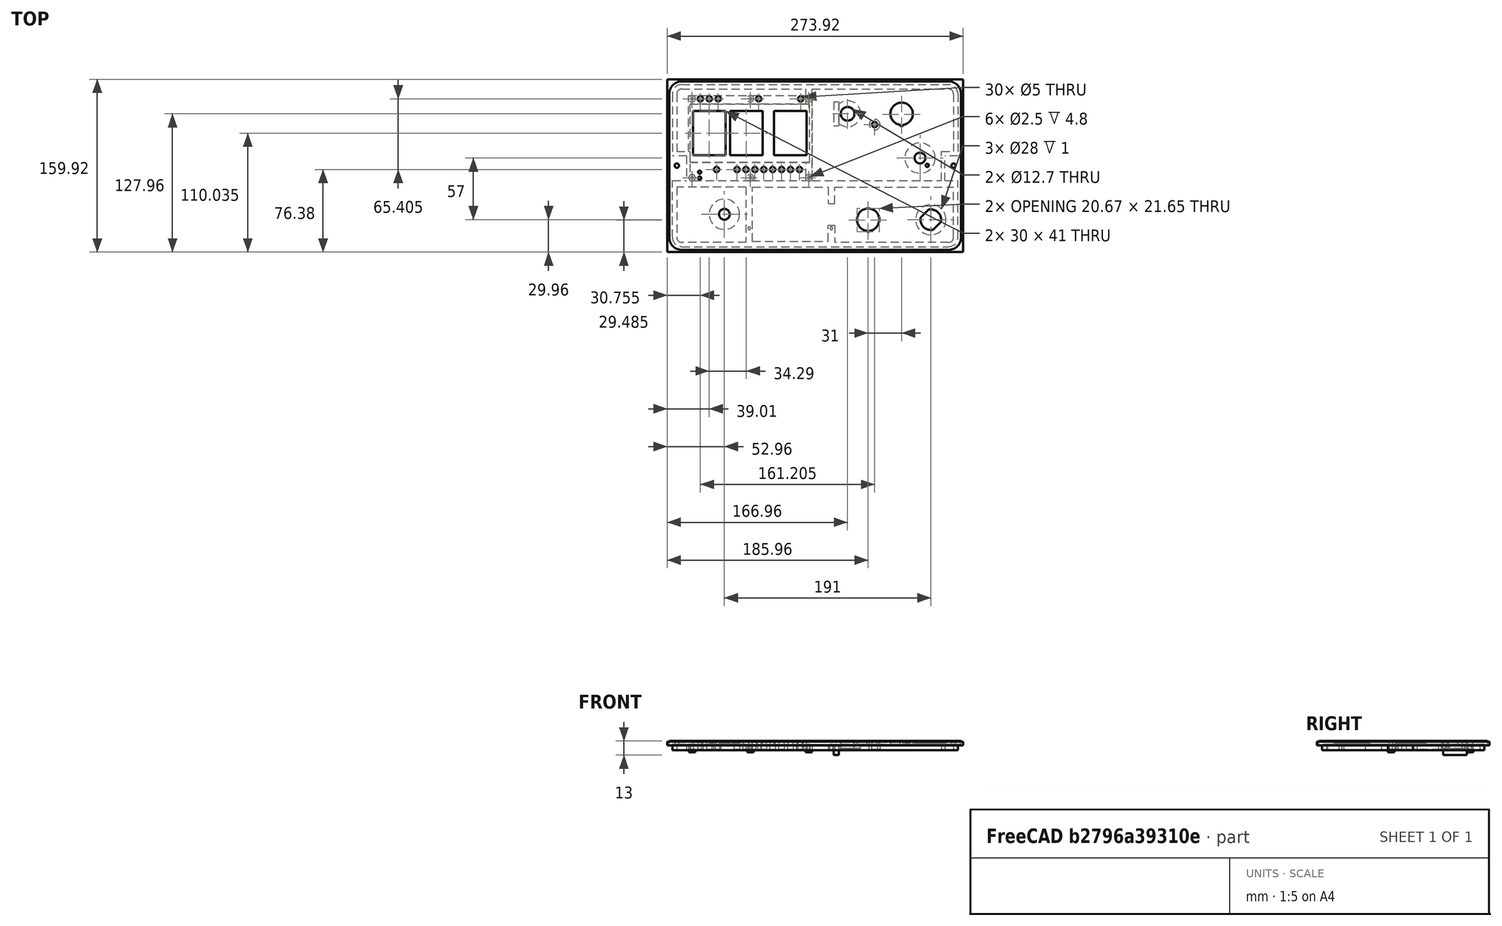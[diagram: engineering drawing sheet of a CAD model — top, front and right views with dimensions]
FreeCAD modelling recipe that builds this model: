
FCSTD DOCUMENT  (FreeCAD 0.18.1R)
Label: telelco_1170_panel
License: All rights reserved
LicenseURL: http://en.wikipedia.org/wiki/All_rights_reserved
objects: Sketcher::SketchObject×9, Part::Extrusion×9, Path::FeaturePython×4, Part::MultiFuse×2, Part::Cut×2, Part::FeaturePython×2, App::FeaturePython×1, Mesh::FeaturePython×1, App::DocumentObjectGroup×1, Path::FeatureCompoundPython×1
note: 26 computed .brp shape members not serialized (recipe doc carries the construction recipe); baked Part::Feature solids carry a one-line shape summary decoded from their .brp

FEATURE [Sketcher::SketchObject] Sketch  label="panel surface"
  MapMode = 5
  sketch-geometry (72):
    g0: Circle CenterX=-84 CenterY=-45 CenterZ=0 NormalX=0 NormalY=0 NormalZ=1 AngleXU=0 Radius=5
    g1: LineSegment [constr] StartX=-117 StartY=65 StartZ=0 EndX=-2.7 EndY=65 EndZ=0
    g2: LineSegment [constr] StartX=-2.7 StartY=65 StartZ=0 EndX=-2.7 EndY=-14.375 EndZ=0
    g3: LineSegment [constr] StartX=-2.7 StartY=-14.375 StartZ=0 EndX=-117 EndY=-14.375 EndZ=0
    g4: LineSegment [constr] StartX=-117 StartY=-14.375 StartZ=0 EndX=-117 EndY=65 EndZ=0
    g5: LineSegment StartX=-112.95 StartY=50.575 StartZ=0 EndX=-82.95 EndY=50.575 EndZ=0
    g6: LineSegment StartX=-82.95 StartY=50.575 StartZ=0 EndX=-82.95 EndY=9.575 EndZ=0
    g7: LineSegment StartX=-82.95 StartY=9.575 StartZ=0 EndX=-112.95 EndY=9.575 EndZ=0
    g8: LineSegment StartX=-112.95 StartY=9.575 StartZ=0 EndX=-112.95 EndY=50.575 EndZ=0
    g9: LineSegment [constr] StartX=-117 StartY=30.075 StartZ=0 EndX=-2.7 EndY=30.075 EndZ=0
    g10: LineSegment [constr] StartX=-97.95 StartY=65 StartZ=0 EndX=-97.95 EndY=-14.375 EndZ=0
    g11: LineSegment [constr] StartX=-63.66 StartY=65 StartZ=0 EndX=-63.66 EndY=-14.375 EndZ=0
    g12: LineSegment StartX=-78.66 StartY=50.575 StartZ=0 EndX=-48.66 EndY=50.575 EndZ=0
    g13: LineSegment StartX=-48.66 StartY=50.575 StartZ=0 EndX=-48.66 EndY=9.575 EndZ=0
    g14: LineSegment StartX=-48.66 StartY=9.575 StartZ=0 EndX=-78.66 EndY=9.575 EndZ=0
    g15: LineSegment StartX=-78.66 StartY=9.575 StartZ=0 EndX=-78.66 EndY=50.575 EndZ=0
    g16: LineSegment [constr] StartX=-23.02 StartY=65 StartZ=0 EndX=-23.02 EndY=-14.375 EndZ=0
    g17: LineSegment StartX=-38.02 StartY=50.575 StartZ=0 EndX=-8.02 EndY=50.575 EndZ=0
    g18: LineSegment StartX=-8.02 StartY=50.575 StartZ=0 EndX=-8.02 EndY=9.575 EndZ=0
    g19: LineSegment StartX=-8.02 StartY=9.575 StartZ=0 EndX=-38.02 EndY=9.575 EndZ=0
    g20: LineSegment StartX=-38.02 StartY=9.575 StartZ=0 EndX=-38.02 EndY=50.575 EndZ=0
    g21: LineSegment [constr] StartX=-117 StartY=61.825 StartZ=0 EndX=-2.7 EndY=61.825 EndZ=0
    g22: Circle CenterX=-106.205 CenterY=61.825 CenterZ=0 NormalX=0 NormalY=0 NormalZ=1 AngleXU=0 Radius=2.5
    g23: Circle CenterX=-97.95 CenterY=61.825 CenterZ=0 NormalX=0 NormalY=0 NormalZ=1 AngleXU=0 Radius=2.5
    g24: Circle CenterX=-89.695 CenterY=61.825 CenterZ=0 NormalX=0 NormalY=0 NormalZ=1 AngleXU=0 Radius=2.5
    g25: Circle CenterX=-52.23 CenterY=61.825 CenterZ=0 NormalX=0 NormalY=0 NormalZ=1 AngleXU=0 Radius=2.5
    g26: Circle CenterX=-13.368 CenterY=61.825 CenterZ=0 NormalX=0 NormalY=0 NormalZ=1 AngleXU=0 Radius=2.5
    g27: LineSegment [constr] StartX=-117 StartY=-3.58 StartZ=0 EndX=-2.7 EndY=-3.58 EndZ=0
    g28: Circle CenterX=-91.219 CenterY=-3.58 CenterZ=0 NormalX=0 NormalY=0 NormalZ=1 AngleXU=0 Radius=2.5
    g29: Circle CenterX=-72.296 CenterY=-3.58 CenterZ=0 NormalX=0 NormalY=0 NormalZ=1 AngleXU=0 Radius=2.5
    g30: Circle CenterX=-64.041 CenterY=-3.58 CenterZ=0 NormalX=0 NormalY=0 NormalZ=1 AngleXU=0 Radius=2.5
    g31: Circle CenterX=-55.786 CenterY=-3.58 CenterZ=0 NormalX=0 NormalY=0 NormalZ=1 AngleXU=0 Radius=2.5
    g32: Circle CenterX=-39.276 CenterY=-3.58 CenterZ=0 NormalX=0 NormalY=0 NormalZ=1 AngleXU=0 Radius=2.5
    g33: Circle CenterX=-22.766 CenterY=-3.58 CenterZ=0 NormalX=0 NormalY=0 NormalZ=1 AngleXU=0 Radius=2.5
    g34: Circle CenterX=-14.511 CenterY=-3.58 CenterZ=0 NormalX=0 NormalY=0 NormalZ=1 AngleXU=0 Radius=2.5
    g35: Circle CenterX=-31.021 CenterY=-3.58 CenterZ=0 NormalX=0 NormalY=0 NormalZ=1 AngleXU=0 Radius=2.5
    g36: Circle CenterX=-47.531 CenterY=-3.58 CenterZ=0 NormalX=0 NormalY=0 NormalZ=1 AngleXU=0 Radius=2.5
    g37: LineSegment [constr] StartX=-106.84 StartY=-3.58 StartZ=0 EndX=-106.84 EndY=-14.375 EndZ=0
    g38: Circle CenterX=-106.84 CenterY=-5.993 CenterZ=0 NormalX=0 NormalY=0 NormalZ=1 AngleXU=0 Radius=1.5
    g39: Circle CenterX=-106.84 CenterY=-11.5556 CenterZ=0 NormalX=0 NormalY=0 NormalZ=1 AngleXU=0 Radius=1.5
    g40: Circle [constr] CenterX=107 CenterY=-50 CenterZ=0 NormalX=0 NormalY=0 NormalZ=1 AngleXU=0 Radius=6.35
    g41: Circle CenterX=97 CenterY=7 CenterZ=0 NormalX=0 NormalY=0 NormalZ=1 AngleXU=0 Radius=5
    g42: Circle CenterX=-128 CenterY=0 CenterZ=0 NormalX=0 NormalY=0 NormalZ=1 AngleXU=0 Radius=2
    g43: Circle CenterX=128 CenterY=0 CenterZ=0 NormalX=0 NormalY=0 NormalZ=1 AngleXU=0 Radius=2
    g44: LineSegment [constr] StartX=30 StartY=48 StartZ=0 EndX=80 EndY=48 EndZ=0
    g45: Circle CenterX=30 CenterY=48 CenterZ=0 NormalX=0 NormalY=0 NormalZ=1 AngleXU=0 Radius=6.35
    g46: LineSegment [constr] StartX=55 StartY=48 StartZ=0 EndX=55 EndY=38 EndZ=0
    g47: Circle CenterX=55 CenterY=38 CenterZ=0 NormalX=0 NormalY=0 NormalZ=1 AngleXU=0 Radius=2.5
    g48: LineSegment [constr] StartX=97 StartY=7 StartZ=0 EndX=103.735 EndY=0.264808 EndZ=0
    g49: Circle CenterX=103.735 CenterY=0.264808 CenterZ=0 NormalX=0 NormalY=0 NormalZ=1 AngleXU=0 Radius=1.5
    g50: LineSegment StartX=47.85 StartY=-61.3 StartZ=0 EndX=50.15 EndY=-61.3 EndZ=0
    g51: LineSegment StartX=50.15 StartY=-61.3 StartZ=0 EndX=50.15 EndY=-60.2859 EndZ=0
    g52: LineSegment StartX=47.85 StartY=-61.3 StartZ=0 EndX=47.85 EndY=-60.2859 EndZ=0
    g53: ArcOfCircle CenterX=49 CenterY=-50 CenterZ=0 NormalX=0 NormalY=0 NormalZ=1 AngleXU=0 Radius=10.35 StartAngle=4.82373 EndAngle=10.8842
    g54: LineSegment StartX=78.85 StartY=36.7 StartZ=0 EndX=81.15 EndY=36.7 EndZ=0
    g55: LineSegment StartX=78.85 StartY=36.7 StartZ=0 EndX=78.85 EndY=37.7141 EndZ=0
    g56: LineSegment StartX=81.15 StartY=36.7 StartZ=0 EndX=81.15 EndY=37.7141 EndZ=0
    g57: ArcOfCircle CenterX=80 CenterY=48 CenterZ=0 NormalX=0 NormalY=0 NormalZ=1 AngleXU=0 Radius=10.35 StartAngle=4.82373 EndAngle=10.8842
    g58: ArcOfCircle CenterX=-123.32 CenterY=66.32 CenterZ=0 NormalX=0 NormalY=0 NormalZ=1 AngleXU=0 Radius=11.68 StartAngle=1.5708 EndAngle=3.14159
    g59: ArcOfCircle CenterX=123.32 CenterY=66.32 CenterZ=0 NormalX=0 NormalY=0 NormalZ=1 AngleXU=0 Radius=11.68 StartAngle=1.037e-13 EndAngle=1.5708
    g60: ArcOfCircle CenterX=123.32 CenterY=-66.32 CenterZ=0 NormalX=0 NormalY=0 NormalZ=1 AngleXU=0 Radius=11.68 StartAngle=4.71239 EndAngle=6.28319
    g61: ArcOfCircle CenterX=-123.32 CenterY=-66.32 CenterZ=0 NormalX=0 NormalY=0 NormalZ=1 AngleXU=0 Radius=11.68 StartAngle=3.14159 EndAngle=4.71239
    g62: LineSegment StartX=-123.32 StartY=78 StartZ=0 EndX=123.32 EndY=78 EndZ=0
    g63: LineSegment StartX=-135 StartY=66.32 StartZ=0 EndX=-135 EndY=-66.32 EndZ=0
    g64: LineSegment StartX=135 StartY=66.32 StartZ=0 EndX=135 EndY=-66.32 EndZ=0
    g65: LineSegment StartX=-123.32 StartY=-78 StartZ=0 EndX=123.32 EndY=-78 EndZ=0
    g66: LineSegment StartX=109.218 StartY=-59.2376 StartZ=0 EndX=116.238 EndY=-52.2176 EndZ=0
    g67: LineSegment StartX=97.7624 StartY=-47.7824 StartZ=0 EndX=104.782 EndY=-40.7624 EndZ=0
    g68: LineSegment [constr] StartX=107 StartY=-50 StartZ=0 EndX=112.728 EndY=-55.7276 EndZ=0
    g69: LineSegment [constr] StartX=107 StartY=-50 StartZ=0 EndX=101.272 EndY=-44.2724 EndZ=0
    g70: ArcOfCircle CenterX=107 CenterY=-50 CenterZ=0 NormalX=0 NormalY=0 NormalZ=1 AngleXU=0 Radius=9.5 StartAngle=6.04758 EndAngle=8.08958
    g71: ArcOfCircle CenterX=107 CenterY=-50 CenterZ=0 NormalX=0 NormalY=0 NormalZ=1 AngleXU=0 Radius=9.5 StartAngle=2.90599 EndAngle=4.94799
  constraints (210):
    c: Radius(g0) = 5
    c: Coincident(g1,g2)
    c: Coincident(g2,g3)
    c: Coincident(g3,g4)
    c: Coincident(g4,g1)
    c: Horizontal(g1)
    c: Horizontal(g3)
    c: Vertical(g2)
    c: Vertical(g4)
    c: DistanceX(g1,g1) = 114.3
    c: DistanceY(g2,g2) = 79.375
    c: Coincident(g5,g6)
    c: Coincident(g6,g7)
    c: Coincident(g7,g8)
    c: Coincident(g8,g5)
    c: Horizontal(g5)
    c: Horizontal(g7)
    c: Vertical(g8)
    c: DistanceX(g7,g7) = 30
    c: DistanceY(g6,g6) = 41
    c: PointOnObject(g9,g4)
    c: PointOnObject(g9,g2)
    c: DistanceY(g9,g1) = 34.925
    c: PointOnObject(g10,g1)
    c: PointOnObject(g10,g3)
    c: DistanceX(g10,g2) = 95.25
    c: Symmetric(g7,g6,g10)
    c: Symmetric(g6,g5,g9)
    c: PointOnObject(g11,g1)
    c: PointOnObject(g11,g3)
    c: Vertical(g11)
    c: DistanceX(g11,g2) = 60.96
    c: Coincident(g12,g13)
    c: Coincident(g13,g14)
    c: Coincident(g14,g15)
    c: Coincident(g15,g12)
    c: Horizontal(g12)
    c: Vertical(g13)
    c: Vertical(g15)
    c: Equal(g14,g7)
    c: Equal(g6,g15)
    c: Symmetric(g14,g13,g11)
    c: Symmetric(g12,g13,g9)
    c: PointOnObject(g16,g1)
    c: PointOnObject(g16,g3)
    c: Vertical(g16)
    c: DistanceX(g16,g2) = 20.32
    c: Coincident(g17,g18)
    c: Coincident(g18,g19)
    c: Coincident(g19,g20)
    c: Coincident(g20,g17)
    c: Horizontal(g17)
    c: Vertical(g20)
    c: Equal(g17,g12)
    c: Equal(g13,g20)
    c: Symmetric(g19,g18,g16)
    c: Symmetric(g18,g17,g9)
    c: PointOnObject(g21,g4)
    c: PointOnObject(g21,g2)
    c: Horizontal(g21)
    c: DistanceY(g21,g1) = 3.175
    c: PointOnObject(g22,g21)
    c: Radius(g22) = 2.5
    c: DistanceX(g22,g21) = 103.505
    c: PointOnObject(g23,g21)
    c: PointOnObject(g24,g21)
    c: PointOnObject(g25,g21)
    c: PointOnObject(g26,g21)
    c: Equal(g22,g23)
    c: Equal(g23,g24)
    c: Equal(g24,g25)
    c: Equal(g25,g26)
    c: DistanceX(g26,g21) = 10.668
    c: DistanceX(g25,g21) = 49.53
    c: DistanceX(g24,g21) = 86.995
    c: DistanceX(g23,g21) = 95.25
    c: PointOnObject(g27,g4)
    c: PointOnObject(g27,g2)
    c: Horizontal(g27)
    c: DistanceY(g27,g1) = 68.58
    c: PointOnObject(g28,g27)
    c: PointOnObject(g29,g27)
    c: PointOnObject(g30,g27)
    c: PointOnObject(g31,g27)
    c: PointOnObject(g32,g27)
    c: PointOnObject(g33,g27)
    c: PointOnObject(g34,g27)
    c: Equal(g28,g29)
    c: Equal(g33,g34)
    c: Equal(g34,g22)
    c: PointOnObject(g35,g27)
    c: PointOnObject(g36,g27)
    c: Equal(g36,g32)
    c: Equal(g32,g35)
    c: DistanceX(g34,g27) = 11.811
    c: DistanceX(g33,g27) = 20.066
    c: DistanceX(g35,g27) = 28.321
    c: DistanceX(g32,g27) = 36.576
    c: DistanceX(g36,g27) = 44.831
    c: DistanceX(g31,g27) = 53.086
    c: DistanceX(g30,g27) = 61.341
    c: DistanceX(g29,g27) = 69.596
    c: DistanceX(g28,g27) = 88.519
    c: PointOnObject(g37,g27)
    c: PointOnObject(g37,g3)
    c: Vertical(g37)
    c: DistanceX(g37,g2) = 104.14
    c: PointOnObject(g38,g37)
    c: PointOnObject(g39,g37)
    c: Equal(g38,g39)
    c: Radius(g38) = 1.5
    c: DistanceY(g38,g1) = 70.993
    c: DistanceY(g39,g1) = 76.5556
    c: Radius(g40) = 6.35
    c: PointOnObject(g42,g-1)
    c: PointOnObject(g43,g-1)
    c: Radius(g42) = 2
    c: Equal(g42,g43)
    c: Horizontal(g44)
    c: Coincident(g45,g44)
    c: Equal(g45,g40)
    c: Equal(g41,g0)
    c: DistanceX(g44,g44) = 50
    c: DistanceY(g-1,g44) = 48
    c: DistanceY(g-1,g1) = 65
    c: Vertical(g46)
    c: DistanceY(g46,g46) = 10
    c: Symmetric(g44,g44,g46)
    c: Coincident(g47,g46)
    c: Equal(g26,g47)
    c: Coincident(g48,g41)
    c: Distance(g48) = 9.525
    c: Angle(g48) = -0.785398
    c: Coincident(g49,g48)
    c: Radius(g49) = 1.5
    c: DistanceY(g40,g-1) = 50
    c: DistanceX(g50,g50) = 2.3
    c: Coincident(g51,g50)
    c: Vertical(g51)
    c: Coincident(g52,g50)
    c: Vertical(g52)
    c: Coincident(g53,g52)
    c: Coincident(g53,g51)
    c: Radius(g53) = 10.35
    c: DistanceY(g50,g53) = 11.3
    c: Horizontal(g54)
    c: DistanceX(g54,g54) = 2.3
    c: DistanceY(g54,g44) = 11.3
    c: Coincident(g55,g54)
    c: Vertical(g55)
    c: Coincident(g56,g54)
    c: Vertical(g56)
    c: Coincident(g57,g44)
    c: Coincident(g57,g55)
    c: Coincident(g57,g56)
    c: Radius(g57) = 10.35
    c: Equal(g33,g35)
    c: Equal(g36,g31)
    c: Equal(g31,g30)
    c: Equal(g30,g29)
    c: DistanceX(g53,g40) = 58
    c: Horizontal(g50)
    c: Horizontal(g52,g51)
    c: Horizontal(g55,g56)
    c: Horizontal(g53,g40)
    c: DistanceX(g2,g-1) = 2.7
    c: DistanceX(g0,g-1) = 84
    c: DistanceY(g0,g-1) = 45
    c: DistanceX(g-1,g53) = 49
    c: DistanceX(g-1,g44) = 30
    c: DistanceX(g-1,g41) = 97
    c: DistanceY(g-1,g41) = 7
    c: DistanceX(g-1,g43) = 128
    c: DistanceX(g42,g-1) = 128
    c: Radius(g58) = 11.68
    c: Equal(g58,g59)
    c: Equal(g59,g60)
    c: Equal(g60,g61)
    c: Horizontal(g62)
    c: Tangent(g59,g62) = 1.5708
    c: Tangent(g62,g58) = 1.5708
    c: Vertical(g64)
    c: Tangent(g64,g59) = 1.5708
    c: Tangent(g63,g58) = -1.5708
    c: DistanceX(g58,g59) = 270
    c: Symmetric(g58,g59,g-2)
    c: Tangent(g63,g61) = -1.5708
    c: Tangent(g65,g61) = -1.5708
    c: DistanceY(g61,g58) = 156
    c: Symmetric(g61,g58,g-1)
    c: Tangent(g60,g65) = -1.5708
    c: Tangent(g60,g64) = 1.5708
    c: Angle(g66,g65) = 2.35619
    c: Parallel(g67,g66)
    c: Coincident(g68,g40)
    c: PointOnObject(g68,g66)
    c: Perpendicular(g68,g66)
    c: Distance(g68) = 8.1
    c: Coincident(g69,g40)
    c: PointOnObject(g69,g67)
    c: Perpendicular(g69,g67)
    c: Equal(g69,g68)
    c: Coincident(g70,g40)
    c: Coincident(g70,g67)
    c: Coincident(g70,g66)
    c: Coincident(g71,g40)
    c: Coincident(g71,g66)
    c: Coincident(g71,g67)
    c: Diameter(g70) = 19
    c: Equal(g71,g70)
FEATURE [Sketcher::SketchObject] Sketch002  label="pcb mounts"
  MapMode = 5
  sketch-geometry (18):
    g0: LineSegment [constr] StartX=-117 StartY=65 StartZ=0 EndX=-2.7 EndY=65 EndZ=0
    g1: LineSegment [constr] StartX=-2.7 StartY=65 StartZ=0 EndX=-2.7 EndY=-14.375 EndZ=0
    g2: LineSegment [constr] StartX=-2.7 StartY=-14.375 StartZ=0 EndX=-117 EndY=-14.375 EndZ=0
    g3: LineSegment [constr] StartX=-117 StartY=-14.375 StartZ=0 EndX=-117 EndY=65 EndZ=0
    g4: LineSegment [constr] StartX=-117 StartY=61.825 StartZ=0 EndX=-2.7 EndY=61.825 EndZ=0
    g5: LineSegment [constr] StartX=-117 StartY=-11.2 StartZ=0 EndX=-2.7 EndY=-11.2 EndZ=0
    g6: Circle CenterX=-5.875 CenterY=61.825 CenterZ=0 NormalX=0 NormalY=0 NormalZ=1 AngleXU=0 Radius=1.25
    g7: Circle CenterX=-5.875 CenterY=61.825 CenterZ=0 NormalX=0 NormalY=0 NormalZ=1 AngleXU=0 Radius=3
    g8: Circle CenterX=-59.85 CenterY=61.825 CenterZ=0 NormalX=0 NormalY=0 NormalZ=1 AngleXU=0 Radius=3
    g9: Circle CenterX=-59.85 CenterY=61.825 CenterZ=0 NormalX=0 NormalY=0 NormalZ=1 AngleXU=0 Radius=1.25
    g10: Circle CenterX=-113.825 CenterY=61.825 CenterZ=0 NormalX=0 NormalY=0 NormalZ=1 AngleXU=0 Radius=1.25
    g11: Circle CenterX=-113.825 CenterY=61.825 CenterZ=0 NormalX=0 NormalY=0 NormalZ=1 AngleXU=0 Radius=3
    g12: Circle CenterX=-113.825 CenterY=-11.2 CenterZ=0 NormalX=0 NormalY=0 NormalZ=1 AngleXU=0 Radius=1.25
    g13: Circle CenterX=-113.825 CenterY=-11.2 CenterZ=0 NormalX=0 NormalY=0 NormalZ=1 AngleXU=0 Radius=3
    g14: Circle CenterX=-59.85 CenterY=-11.2 CenterZ=0 NormalX=0 NormalY=0 NormalZ=1 AngleXU=0 Radius=1.25
    g15: Circle CenterX=-59.85 CenterY=-11.2 CenterZ=0 NormalX=0 NormalY=0 NormalZ=1 AngleXU=0 Radius=3
    g16: Circle CenterX=-5.875 CenterY=-11.2 CenterZ=0 NormalX=0 NormalY=0 NormalZ=1 AngleXU=0 Radius=1.25
    g17: Circle CenterX=-5.875 CenterY=-11.2 CenterZ=0 NormalX=0 NormalY=0 NormalZ=1 AngleXU=0 Radius=3
  constraints (50):
    c: Coincident(g1,g2)
    c: Coincident(g2,g3)
    c: Coincident(g3,g0)
    c: Horizontal(g0)
    c: Horizontal(g2)
    c: Vertical(g1)
    c: Vertical(g3)
    c: DistanceX(g0,g0) = 114.3
    c: DistanceY(g1,g1) = 79.375
    c: PointOnObject(g4,g3)
    c: PointOnObject(g4,g1)
    c: Horizontal(g4)
    c: DistanceY(g4,g0) = 3.175
    c: PointOnObject(g5,g3)
    c: PointOnObject(g5,g1)
    c: Horizontal(g5)
    c: DistanceY(g5,g0) = 76.2
    c: DistanceX(g1,g-1) = 2.7
    c: Coincident(g1,g0)
    c: DistanceY(g-1,g0) = 65
    c: PointOnObject(g6,g4)
    c: Radius(g6) = 1.25
    c: Coincident(g7,g6)
    c: Radius(g7) = 3
    c: DistanceX(g6,g4) = 3.175
    c: PointOnObject(g8,g4)
    c: Coincident(g9,g8)
    c: Equal(g9,g6)
    c: Equal(g8,g7)
    c: DistanceX(g8,g4) = 57.15
    c: PointOnObject(g10,g4)
    c: Coincident(g11,g10)
    c: Equal(g10,g9)
    c: Equal(g11,g8)
    c: DistanceX(g10,g4) = 111.125
    c: PointOnObject(g12,g5)
    c: Coincident(g13,g12)
    c: Equal(g12,g10)
    c: Equal(g13,g11)
    c: PointOnObject(g14,g5)
    c: Coincident(g15,g14)
    c: PointOnObject(g16,g5)
    c: Coincident(g17,g16)
    c: Equal(g14,g9)
    c: Equal(g8,g15)
    c: Equal(g6,g16)
    c: Equal(g7,g17)
    c: Vertical(g8,g14)
    c: Vertical(g10,g12)
    c: Vertical(g6,g16)
FEATURE [Part::Extrusion] Extrude002  label="Extrude pcb mounts"
  Base = -> Sketch002
  Dir = (0,0,1)
  DirMode = 2
  FaceMakerClass = Part::FaceMakerBullseye
  LengthFwd = 7.5
  LengthRev = 0
  Reversed = true
  Solid = true
  Symmetric = false
FEATURE [Sketcher::SketchObject] Sketch003  label="ribs"
  MapMode = 5
  sketch-geometry (60):
    g0: LineSegment [constr] StartX=-123.32 StartY=78 StartZ=0 EndX=123.32 EndY=78 EndZ=0
    g1: LineSegment [constr] StartX=-123.32 StartY=-78 StartZ=0 EndX=123.32 EndY=-78 EndZ=0
    g2: LineSegment [constr] StartX=-135 StartY=-66.32 StartZ=0 EndX=-135 EndY=66.32 EndZ=0
    g3: ArcOfCircle [constr] CenterX=-123.32 CenterY=66.32 CenterZ=0 NormalX=0 NormalY=0 NormalZ=1 AngleXU=0 Radius=11.68 StartAngle=1.5708 EndAngle=3.14159
    g4: ArcOfCircle [constr] CenterX=123.32 CenterY=66.32 CenterZ=0 NormalX=0 NormalY=0 NormalZ=1 AngleXU=0 Radius=11.68 StartAngle=-1.039e-13 EndAngle=1.5708
    g5: ArcOfCircle [constr] CenterX=123.32 CenterY=-66.32 CenterZ=0 NormalX=0 NormalY=0 NormalZ=1 AngleXU=0 Radius=11.68 StartAngle=4.71239 EndAngle=6.28319
    g6: ArcOfCircle [constr] CenterX=-123.32 CenterY=-66.32 CenterZ=0 NormalX=0 NormalY=0 NormalZ=1 AngleXU=0 Radius=11.68 StartAngle=3.14159 EndAngle=4.71239
    g7: ArcOfCircle CenterX=123.32 CenterY=66.32 CenterZ=0 NormalX=0 NormalY=0 NormalZ=1 AngleXU=0 Radius=4.68 StartAngle=4e-16 EndAngle=1.5708
    g8: ArcOfCircle CenterX=-123.32 CenterY=66.32 CenterZ=0 NormalX=0 NormalY=0 NormalZ=1 AngleXU=0 Radius=4.68 StartAngle=1.5708 EndAngle=3.14159
    g9: ArcOfCircle CenterX=-123.32 CenterY=-66.32 CenterZ=0 NormalX=0 NormalY=0 NormalZ=1 AngleXU=0 Radius=4.68 StartAngle=3.14159 EndAngle=4.71239
    g10: LineSegment StartX=-119 StartY=9 StartZ=0 EndX=-119 EndY=-14 EndZ=0
    g11: LineSegment StartX=-128 StartY=66.32 StartZ=0 EndX=-128 EndY=13 EndZ=0
    g12: LineSegment [constr] StartX=135 StartY=-66.32 StartZ=0 EndX=135 EndY=66.32 EndZ=0
    g13: LineSegment StartX=-64 StartY=-71 StartZ=0 EndX=-123.32 EndY=-71 EndZ=0
    g14: LineSegment StartX=-2.7 StartY=71 StartZ=0 EndX=123.32 EndY=71 EndZ=0
    g15: LineSegment StartX=-128 StartY=-20 StartZ=0 EndX=-128 EndY=-66.32 EndZ=0
    g16: LineSegment StartX=-123.32 StartY=71 StartZ=0 EndX=-8.7 EndY=71 EndZ=0
    g17: LineSegment StartX=-116 StartY=-14 StartZ=0 EndX=-8.7 EndY=-14 EndZ=0
    g18: LineSegment StartX=-2.7 StartY=-14 StartZ=0 EndX=-2.7 EndY=71 EndZ=0
    g19: LineSegment StartX=-8.7 StartY=-14 StartZ=0 EndX=-8.7 EndY=71 EndZ=0
    g20: LineSegment StartX=-58 StartY=-70 StartZ=0 EndX=12 EndY=-70 EndZ=0
    g21: LineSegment StartX=12 StartY=-70 StartZ=0 EndX=12 EndY=-55 EndZ=0
    g22: LineSegment StartX=12 StartY=-20 StartZ=0 EndX=12 EndY=-35 EndZ=0
    g23: LineSegment StartX=-58 StartY=-70 StartZ=0 EndX=-58 EndY=-20 EndZ=0
    g24: LineSegment StartX=-64 StartY=-20 StartZ=0 EndX=-64 EndY=-71 EndZ=0
    g25: LineSegment StartX=-58 StartY=-20 StartZ=0 EndX=12 EndY=-20 EndZ=0
    g26: LineSegment StartX=-64 StartY=-20 StartZ=0 EndX=-128 EndY=-20 EndZ=0
    g27: LineSegment StartX=18 StartY=-55 StartZ=0 EndX=18 EndY=-71 EndZ=0
    g28: LineSegment StartX=12 StartY=-55 StartZ=0 EndX=18 EndY=-55 EndZ=0
    g29: ArcOfCircle CenterX=123.32 CenterY=-66.32 CenterZ=0 NormalX=0 NormalY=0 NormalZ=1 AngleXU=0 Radius=4.68 StartAngle=4.71239 EndAngle=6.28319
    g30: LineSegment StartX=128 StartY=-66.32 StartZ=0 EndX=128 EndY=-20 EndZ=0
    g31: LineSegment StartX=123.32 StartY=-71 StartZ=0 EndX=18 EndY=-71 EndZ=0
    g32: LineSegment StartX=12 StartY=-35 StartZ=0 EndX=18 EndY=-35 EndZ=0
    g33: LineSegment StartX=18 StartY=-35 StartZ=0 EndX=18 EndY=-20 EndZ=0
    g34: LineSegment StartX=18 StartY=-20 StartZ=0 EndX=128 EndY=-20 EndZ=0
    g35: Circle CenterX=-5.875 CenterY=61.825 CenterZ=0 NormalX=0 NormalY=0 NormalZ=1 AngleXU=0 Radius=1.25
    g36: Circle CenterX=-5.875 CenterY=-11.2 CenterZ=0 NormalX=0 NormalY=0 NormalZ=1 AngleXU=0 Radius=1.25
    g37: Circle CenterX=-61 CenterY=-58 CenterZ=0 NormalX=0 NormalY=0 NormalZ=1 AngleXU=0 Radius=1.25
    g38: Circle CenterX=15 CenterY=-58 CenterZ=0 NormalX=0 NormalY=0 NormalZ=1 AngleXU=0 Radius=1.25
    g39: LineSegment StartX=-123.32 StartY=-75 StartZ=0 EndX=123.32 EndY=-75 EndZ=0
    g40: LineSegment StartX=-123.32 StartY=75 StartZ=0 EndX=123.32 EndY=75 EndZ=0
    g41: ArcOfCircle CenterX=123.32 CenterY=-66.32 CenterZ=0 NormalX=0 NormalY=0 NormalZ=1 AngleXU=0 Radius=8.68 StartAngle=4.71239 EndAngle=6.28319
    g42: ArcOfCircle CenterX=-123.32 CenterY=-66.32 CenterZ=0 NormalX=0 NormalY=0 NormalZ=1 AngleXU=0 Radius=8.68 StartAngle=3.14159 EndAngle=4.71239
    g43: ArcOfCircle CenterX=123.32 CenterY=66.32 CenterZ=0 NormalX=0 NormalY=0 NormalZ=1 AngleXU=0 Radius=8.68 StartAngle=-2.1239e-11 EndAngle=1.5708
    g44: ArcOfCircle CenterX=-123.32 CenterY=66.32 CenterZ=0 NormalX=0 NormalY=0 NormalZ=1 AngleXU=0 Radius=8.68 StartAngle=1.5708 EndAngle=3.14159
    g45: LineSegment StartX=132 StartY=66.32 StartZ=0 EndX=132 EndY=9 EndZ=0
    g46: LineSegment StartX=120 StartY=-14 StartZ=0 EndX=120 EndY=9 EndZ=0
    g47: LineSegment StartX=132 StartY=9 StartZ=0 EndX=120 EndY=9 EndZ=0
    g48: LineSegment StartX=117 StartY=-14 StartZ=0 EndX=117 EndY=13 EndZ=0
    g49: LineSegment StartX=117 StartY=13 StartZ=0 EndX=128 EndY=13 EndZ=0
    g50: LineSegment StartX=128 StartY=66.32 StartZ=0 EndX=128 EndY=13 EndZ=0
    g51: LineSegment StartX=-2.7 StartY=-14 StartZ=0 EndX=117 EndY=-14 EndZ=0
    g52: LineSegment StartX=120 StartY=-14 StartZ=0 EndX=132 EndY=-14 EndZ=0
    g53: LineSegment StartX=132 StartY=-66.32 StartZ=0 EndX=132 EndY=-14 EndZ=0
    g54: LineSegment StartX=-132 StartY=66.32 StartZ=0 EndX=-132 EndY=9 EndZ=0
    g55: LineSegment StartX=-119 StartY=9 StartZ=0 EndX=-132 EndY=9 EndZ=0
    g56: LineSegment StartX=-128 StartY=13 StartZ=0 EndX=-116 EndY=13 EndZ=0
    g57: LineSegment StartX=-116 StartY=13 StartZ=0 EndX=-116 EndY=-14 EndZ=0
    g58: LineSegment StartX=-132 StartY=-66.32 StartZ=0 EndX=-132 EndY=-14 EndZ=0
    g59: LineSegment StartX=-132 StartY=-14 StartZ=0 EndX=-119 EndY=-14 EndZ=0
  constraints (158):
    c: Horizontal(g0)
    c: Equal(g0,g1)
    c: Equal(g3,g6)
    c: Equal(g6,g5)
    c: Equal(g5,g4)
    c: Radius(g4) = 11.68
    c: DistanceY(g1,g0) = 156
    c: DistanceX(g2,g5) = 270
    c: Symmetric(g2,g5,g-2)
    c: Symmetric(g1,g0,g-1)
    c: Coincident(g7,g4)
    c: Radius(g7) = 4.68
    c: Coincident(g8,g3)
    c: Coincident(g9,g6)
    c: DistanceX(g2,g10) = 16
    c: Vertical(g11)
    c: Tangent(g11,g8) = -1.5708
    c: Tangent(g12,g4) = -1.5708
    c: Tangent(g12,g5) = -1.5708
    c: Tangent(g6,g2) = 1.5708
    c: Tangent(g6,g1) = -1.5708
    c: Tangent(g3,g2) = 1.5708
    c: Tangent(g3,g0) = 1.5708
    c: Tangent(g4,g0) = 1.5708
    c: Tangent(g5,g1) = -1.5708
    c: Horizontal(g13)
    c: Horizontal(g14)
    c: Vertical(g15)
    c: Tangent(g15,g9) = -1.5708
    c: Tangent(g14,g7) = 1.5708
    c: Tangent(g13,g9) = 1.5708
    c: Horizontal(g16,g14)
    c: Tangent(g16,g8) = 1.5708
    c: Horizontal(g17)
    c: DistanceY(g17,g-1) = 14
    c: DistanceX(g18,g-1) = 2.7
    c: PointOnObject(g18,g16)
    c: Vertical(g18)
    c: Coincident(g14,g18)
    c: DistanceX(g16,g14) = 6
    c: Coincident(g19,g17)
    c: Vertical(g19)
    c: Coincident(g19,g16)
    c: Horizontal(g20)
    c: DistanceX(g20,g20) = 70
    c: Coincident(g21,g20)
    c: Vertical(g21)
    c: DistanceY(g21,g21) = 15
    c: DistanceY(g20,g22) = 50
    c: DistanceY(g22,g-1) = 20
    c: Vertical(g22)
    c: DistanceY(g22,g22) = 15
    c: Vertical(g21,g22)
    c: Horizontal(g13,g27)
    c: Coincident(g23,g20)
    c: Vertical(g23)
    c: Vertical(g24)
    c: DistanceX(g24,g23) = 6
    c: Coincident(g25,g23)
    c: Coincident(g25,g22)
    c: Coincident(g26,g24)
    c: Coincident(g26,g15)
    c: Horizontal(g26)
    c: Horizontal(g24,g23)
    c: Coincident(g13,g24)
    c: Vertical(g27)
    c: Horizontal(g21,g27)
    c: Coincident(g28,g21)
    c: Coincident(g28,g27)
    c: DistanceX(g28,g28) = 6
    c: Horizontal(g17,g52)
    c: Coincident(g29,g5)
    c: Vertical(g30)
    c: Horizontal(g31)
    c: Tangent(g31,g29) = 1.5708
    c: Tangent(g30,g29) = -1.5708
    c: Coincident(g31,g27)
    c: DistanceX(g26,g26) = 64
    c: Coincident(g32,g22)
    c: Horizontal(g32)
    c: Equal(g28,g32)
    c: Coincident(g33,g32)
    c: Vertical(g33)
    c: Equal(g22,g33)
    c: Coincident(g34,g33)
    c: Horizontal(g34)
    c: Coincident(g30,g34)
    c: Equal(g35,g36)
    c: Radius(g35) = 1.25
    c: Vertical(g35,g36)
    c: DistanceX(g36,g-1) = 5.875
    c: DistanceY(g36,g-1) = 11.2
    c: DistanceY(g-1,g35) = 61.825
    c: Diameter(g37) = 2.5
    c: Equal(g37,g38)
    c: Distance(g38,g27) = 3
    c: Distance(g37,g23) = 3
    c: Distance(g38,g28) = 3
    c: DistanceY(g38,g37) = 0
    c: Horizontal(g25)
    c: Horizontal(g39)
    c: DistanceY(g39,g-1) = 75
    c: Horizontal(g40)
    c: Coincident(g41,g29)
    c: Coincident(g42,g9)
    c: Coincident(g43,g7)
    c: Coincident(g44,g8)
    c: Distance(g45,g12) = 3
    c: Vertical(g46)
    c: Coincident(g47,g46)
    c: Horizontal(g47)
    c: DistanceX(g46,g45) = 12
    c: Vertical(g48)
    c: Coincident(g49,g48)
    c: Horizontal(g49)
    c: Coincident(g50,g49)
    c: Vertical(g50)
    c: DistanceX(g48,g46) = 3
    c: DistanceY(g46,g48) = 4
    c: Coincident(g47,g45)
    c: Coincident(g51,g18)
    c: Coincident(g51,g48)
    c: Horizontal(g51)
    c: Coincident(g52,g46)
    c: Horizontal(g52)
    c: DistanceY(g-1,g45) = 9
    c: Coincident(g53,g52)
    c: Vertical(g53)
    c: DistanceY(g46,g48) = 0
    c: Distance(g10,g-1) = 9
    c: Vertical(g10)
    c: Vertical(g54)
    c: Coincident(g55,g10)
    c: Coincident(g55,g54)
    c: Horizontal(g55)
    c: Coincident(g56,g11)
    c: Horizontal(g56)
    c: Coincident(g57,g56)
    c: Vertical(g57)
    c: DistanceY(g10,g56) = 4
    c: DistanceX(g10,g56) = 3
    c: Coincident(g17,g57)
    c: Vertical(g58)
    c: Coincident(g59,g58)
    c: Coincident(g59,g10)
    c: Horizontal(g59)
    c: DistanceX(g2,g44) = 3
    c: Equal(g9,g8)
    c: DistanceY(g17,g10) = 0
    c: Tangent(g50,g7) = 1.5708
    c: Tangent(g45,g43) = 1.5708
    c: Tangent(g43,g40) = 1.5708
    c: Tangent(g53,g41) = -1.5708
    c: Tangent(g41,g39) = -1.5708
    c: Tangent(g42,g39) = -1.5708
    c: Tangent(g58,g42) = 1.5708
    c: Tangent(g54,g44) = -1.5708
    c: Tangent(g44,g40) = 1.5708
FEATURE [Sketcher::SketchObject] Sketch004  label="lcd + led nibs"
  MapMode = 5
  sketch-geometry (48):
    g0: LineSegment StartX=-117 StartY=65 StartZ=0 EndX=-2.7 EndY=65 EndZ=0
    g1: LineSegment StartX=-2.7 StartY=65 StartZ=0 EndX=-2.7 EndY=-14.375 EndZ=0
    g2: LineSegment StartX=-2.7 StartY=-14.375 StartZ=0 EndX=-117 EndY=-14.375 EndZ=0
    g3: LineSegment StartX=-117 StartY=-14.375 StartZ=0 EndX=-117 EndY=65 EndZ=0
    g4: LineSegment StartX=-112.95 StartY=50.575 StartZ=0 EndX=-82.95 EndY=50.575 EndZ=0
    g5: LineSegment StartX=-82.95 StartY=50.575 StartZ=0 EndX=-82.95 EndY=9.575 EndZ=0
    g6: LineSegment StartX=-82.95 StartY=9.575 StartZ=0 EndX=-112.95 EndY=9.575 EndZ=0
    g7: LineSegment StartX=-112.95 StartY=9.575 StartZ=0 EndX=-112.95 EndY=50.575 EndZ=0
    g8: LineSegment [constr] StartX=-117 StartY=30.075 StartZ=0 EndX=-2.7 EndY=30.075 EndZ=0
    g9: LineSegment [constr] StartX=-97.95 StartY=65 StartZ=0 EndX=-97.95 EndY=-14.375 EndZ=0
    g10: LineSegment [constr] StartX=-63.66 StartY=65 StartZ=0 EndX=-63.66 EndY=-14.375 EndZ=0
    g11: LineSegment StartX=-78.66 StartY=50.575 StartZ=0 EndX=-48.66 EndY=50.575 EndZ=0
    g12: LineSegment StartX=-48.66 StartY=50.575 StartZ=0 EndX=-48.66 EndY=9.575 EndZ=0
    g13: LineSegment StartX=-48.66 StartY=9.575 StartZ=0 EndX=-78.66 EndY=9.575 EndZ=0
    g14: LineSegment StartX=-78.66 StartY=9.575 StartZ=0 EndX=-78.66 EndY=50.575 EndZ=0
    g15: LineSegment [constr] StartX=-23.02 StartY=65 StartZ=0 EndX=-23.02 EndY=-14.375 EndZ=0
    g16: LineSegment StartX=-38.02 StartY=50.575 StartZ=0 EndX=-8.02 EndY=50.575 EndZ=0
    g17: LineSegment StartX=-8.02 StartY=50.575 StartZ=0 EndX=-8.02 EndY=9.575 EndZ=0
    g18: LineSegment StartX=-8.02 StartY=9.575 StartZ=0 EndX=-38.02 EndY=9.575 EndZ=0
    g19: LineSegment StartX=-38.02 StartY=9.575 StartZ=0 EndX=-38.02 EndY=50.575 EndZ=0
    g20: LineSegment [constr] StartX=-117 StartY=61.825 StartZ=0 EndX=-2.7 EndY=61.825 EndZ=0
    g21: Circle CenterX=-106.205 CenterY=61.825 CenterZ=0 NormalX=0 NormalY=0 NormalZ=1 AngleXU=0 Radius=2.5
    g22: Circle CenterX=-97.95 CenterY=61.825 CenterZ=0 NormalX=0 NormalY=0 NormalZ=1 AngleXU=0 Radius=2.5
    g23: Circle CenterX=-89.695 CenterY=61.825 CenterZ=0 NormalX=0 NormalY=0 NormalZ=1 AngleXU=0 Radius=2.5
    g24: Circle CenterX=-52.23 CenterY=61.825 CenterZ=0 NormalX=0 NormalY=0 NormalZ=1 AngleXU=0 Radius=2.5
    g25: Circle CenterX=-13.368 CenterY=61.825 CenterZ=0 NormalX=0 NormalY=0 NormalZ=1 AngleXU=0 Radius=2.5
    g26: LineSegment [constr] StartX=-117 StartY=-3.58 StartZ=0 EndX=-2.7 EndY=-3.58 EndZ=0
    g27: Circle CenterX=-91.219 CenterY=-3.58 CenterZ=0 NormalX=0 NormalY=0 NormalZ=1 AngleXU=0 Radius=2.5
    g28: Circle CenterX=-72.296 CenterY=-3.58 CenterZ=0 NormalX=0 NormalY=0 NormalZ=1 AngleXU=0 Radius=2.5
    g29: Circle CenterX=-64.041 CenterY=-3.58 CenterZ=0 NormalX=0 NormalY=0 NormalZ=1 AngleXU=0 Radius=2.5
    g30: Circle CenterX=-55.786 CenterY=-3.58 CenterZ=0 NormalX=0 NormalY=0 NormalZ=1 AngleXU=0 Radius=2.5
    g31: Circle CenterX=-39.276 CenterY=-3.58 CenterZ=0 NormalX=0 NormalY=0 NormalZ=1 AngleXU=0 Radius=2.5
    g32: Circle CenterX=-22.766 CenterY=-3.58 CenterZ=0 NormalX=0 NormalY=0 NormalZ=1 AngleXU=0 Radius=2.5
    g33: Circle CenterX=-14.511 CenterY=-3.58 CenterZ=0 NormalX=0 NormalY=0 NormalZ=1 AngleXU=0 Radius=2.5
    g34: Circle CenterX=-31.021 CenterY=-3.58 CenterZ=0 NormalX=0 NormalY=0 NormalZ=1 AngleXU=0 Radius=2.5
    g35: Circle CenterX=-47.531 CenterY=-3.58 CenterZ=0 NormalX=0 NormalY=0 NormalZ=1 AngleXU=0 Radius=2.5
    g36: LineSegment [constr] StartX=-106.84 StartY=-3.58 StartZ=0 EndX=-106.84 EndY=-14.375 EndZ=0
    g37: Circle CenterX=-106.84 CenterY=-5.993 CenterZ=0 NormalX=0 NormalY=0 NormalZ=1 AngleXU=0 Radius=1.5
    g38: Circle CenterX=-106.84 CenterY=-11.5556 CenterZ=0 NormalX=0 NormalY=0 NormalZ=1 AngleXU=0 Radius=1.5
    g39: Circle CenterX=55 CenterY=38 CenterZ=0 NormalX=0 NormalY=0 NormalZ=1 AngleXU=0 Radius=2.5
    g40: Circle CenterX=55 CenterY=38 CenterZ=0 NormalX=0 NormalY=0 NormalZ=1 AngleXU=0 Radius=5
    g41: Circle CenterX=-113.825 CenterY=61.825 CenterZ=0 NormalX=0 NormalY=0 NormalZ=1 AngleXU=0 Radius=1.25
    g42: Circle CenterX=-59.85 CenterY=61.825 CenterZ=0 NormalX=0 NormalY=0 NormalZ=1 AngleXU=0 Radius=1.25
    g43: Circle CenterX=-5.875 CenterY=61.825 CenterZ=0 NormalX=0 NormalY=0 NormalZ=1 AngleXU=0 Radius=1.25
    g44: LineSegment [constr] StartX=-117 StartY=-11.2 StartZ=0 EndX=-2.7 EndY=-11.2 EndZ=0
    g45: Circle CenterX=-113.825 CenterY=-11.2 CenterZ=0 NormalX=0 NormalY=0 NormalZ=1 AngleXU=0 Radius=1.25
    g46: Circle CenterX=-59.85 CenterY=-11.2 CenterZ=0 NormalX=0 NormalY=0 NormalZ=1 AngleXU=0 Radius=1.25
    g47: Circle CenterX=-5.875 CenterY=-11.2 CenterZ=0 NormalX=0 NormalY=0 NormalZ=1 AngleXU=0 Radius=1.25
  constraints (150):
    c: Coincident(g0,g1)
    c: Coincident(g1,g2)
    c: Coincident(g2,g3)
    c: Coincident(g3,g0)
    c: Horizontal(g0)
    c: Horizontal(g2)
    c: Vertical(g1)
    c: Vertical(g3)
    c: DistanceX(g0,g0) = 114.3
    c: DistanceY(g1,g1) = 79.375
    c: Coincident(g4,g5)
    c: Coincident(g5,g6)
    c: Coincident(g6,g7)
    c: Coincident(g7,g4)
    c: Horizontal(g4)
    c: Horizontal(g6)
    c: Vertical(g5)
    c: Vertical(g7)
    c: DistanceX(g6,g6) = 30
    c: DistanceY(g5,g5) = 41
    c: PointOnObject(g8,g3)
    c: PointOnObject(g8,g1)
    c: DistanceY(g8,g0) = 34.925
    c: PointOnObject(g9,g0)
    c: PointOnObject(g9,g2)
    c: Vertical(g9)
    c: DistanceX(g9,g1) = 95.25
    c: Symmetric(g6,g5,g9)
    c: Symmetric(g5,g4,g8)
    c: PointOnObject(g10,g0)
    c: PointOnObject(g10,g2)
    c: Vertical(g10)
    c: DistanceX(g10,g1) = 60.96
    c: Coincident(g11,g12)
    c: Coincident(g12,g13)
    c: Coincident(g13,g14)
    c: Coincident(g14,g11)
    c: Horizontal(g11)
    c: Horizontal(g13)
    c: Vertical(g12)
    c: Vertical(g14)
    c: Equal(g13,g6)
    c: Equal(g5,g14)
    c: Symmetric(g13,g12,g10)
    c: Symmetric(g11,g12,g8)
    c: PointOnObject(g15,g0)
    c: PointOnObject(g15,g2)
    c: Vertical(g15)
    c: DistanceX(g15,g1) = 20.32
    c: Coincident(g16,g17)
    c: Coincident(g17,g18)
    c: Coincident(g18,g19)
    c: Coincident(g19,g16)
    c: Horizontal(g16)
    c: Horizontal(g18)
    c: Vertical(g17)
    c: Vertical(g19)
    c: Equal(g16,g11)
    c: Equal(g12,g19)
    c: Symmetric(g18,g17,g15)
    c: Symmetric(g17,g16,g8)
    c: PointOnObject(g20,g3)
    c: PointOnObject(g20,g1)
    c: Horizontal(g20)
    c: DistanceY(g20,g0) = 3.175
    c: PointOnObject(g21,g20)
    c: Radius(g21) = 2.5
    c: DistanceX(g21,g20) = 103.505
    c: PointOnObject(g22,g20)
    c: PointOnObject(g23,g20)
    c: PointOnObject(g24,g20)
    c: PointOnObject(g25,g20)
    c: Equal(g21,g22)
    c: Equal(g22,g23)
    c: Equal(g23,g24)
    c: Equal(g24,g25)
    c: DistanceX(g25,g20) = 10.668
    c: DistanceX(g24,g20) = 49.53
    c: DistanceX(g23,g20) = 86.995
    c: DistanceX(g22,g20) = 95.25
    c: PointOnObject(g26,g3)
    c: PointOnObject(g26,g1)
    c: Horizontal(g26)
    c: DistanceY(g26,g0) = 68.58
    c: PointOnObject(g27,g26)
    c: PointOnObject(g28,g26)
    c: PointOnObject(g29,g26)
    c: PointOnObject(g30,g26)
    c: PointOnObject(g31,g26)
    c: PointOnObject(g32,g26)
    c: PointOnObject(g33,g26)
    c: Equal(g27,g28)
    c: Equal(g28,g29)
    c: Equal(g32,g33)
    c: Equal(g33,g21)
    c: PointOnObject(g34,g26)
    c: PointOnObject(g35,g26)
    c: Equal(g35,g31)
    c: Equal(g27,g35)
    c: Equal(g31,g34)
    c: DistanceX(g33,g26) = 11.811
    c: DistanceX(g32,g26) = 20.066
    c: DistanceX(g34,g26) = 28.321
    c: DistanceX(g31,g26) = 36.576
    c: DistanceX(g35,g26) = 44.831
    c: DistanceX(g30,g26) = 53.086
    c: DistanceX(g29,g26) = 61.341
    c: DistanceX(g28,g26) = 69.596
    c: DistanceX(g27,g26) = 88.519
    c: PointOnObject(g36,g26)
    c: PointOnObject(g36,g2)
    c: Vertical(g36)
    c: DistanceX(g36,g1) = 104.14
    c: PointOnObject(g37,g36)
    c: PointOnObject(g38,g36)
    c: Equal(g37,g38)
    c: Radius(g37) = 1.5
    c: DistanceY(g37,g0) = 70.993
    c: DistanceY(g38,g0) = 76.5556
    c: DistanceY(g-1,g0) = 65
    c: Equal(g25,g39)
    c: DistanceX(g-1,g39) = 55
    c: DistanceY(g-1,g39) = 38
    c: Coincident(g40,g39)
    c: Radius(g40) = 5
    c: PointOnObject(g41,g20)
    c: PointOnObject(g42,g20)
    c: PointOnObject(g43,g20)
    c: Radius(g43) = 1.25
    c: Equal(g43,g42)
    c: Equal(g42,g41)
    c: DistanceX(g43,g0) = 3.175
    c: DistanceX(g42,g0) = 57.15
    c: DistanceX(g41,g0) = 111.125
    c: PointOnObject(g44,g3)
    c: PointOnObject(g44,g1)
    c: Horizontal(g44)
    c: DistanceY(g1,g44) = 3.175
    c: PointOnObject(g45,g44)
    c: PointOnObject(g46,g44)
    c: PointOnObject(g47,g44)
    c: Equal(g43,g46)
    c: Equal(g46,g45)
    c: Vertical(g43,g47)
    c: Vertical(g42,g46)
    c: Vertical(g41,g45)
    c: DistanceX(g1,g-1) = 2.7
    c: Equal(g43,g47)
    c: Equal(g29,g30)
    c: Equal(g34,g32)
FEATURE [Part::Extrusion] Extrude005  label="Extrude lcd + led nibs"
  Base = -> Sketch004
  Dir = (0,0,1)
  DirMode = 2
  FaceMakerClass = Part::FaceMakerBullseye
  LengthFwd = 4.8
  LengthRev = 0
  Reversed = true
  Solid = true
  Symmetric = false
FEATURE [Part::Extrusion] Extrude  label="Extrude ribs"
  Base = -> Sketch003
  Dir = (0,0,1)
  DirMode = 2
  FaceMakerClass = Part::FaceMakerBullseye
  LengthFwd = 5.4
  LengthRev = 0
  Reversed = true
  Solid = true
  Symmetric = false
FEATURE [Sketcher::SketchObject] Sketch005  label="toggle switch lands"
  MapMode = 5
  sketch-geometry (2):
    g0: Circle CenterX=30 CenterY=48 CenterZ=0 NormalX=0 NormalY=0 NormalZ=1 AngleXU=0 Radius=6.35
    g1: Circle CenterX=30 CenterY=48 CenterZ=0 NormalX=0 NormalY=0 NormalZ=1 AngleXU=0 Radius=12
  constraints (5):
    c: DistanceX(g-1,g0) = 30
    c: DistanceY(g-1,g0) = 48
    c: Coincident(g1,g0)
    c: Radius(g1) = 12
    c: Radius(g0) = 6.35
FEATURE [Part::Extrusion] Extrude006  label="Extrude toggle switch lands"
  Base = -> Sketch005
  Dir = (0,0,1)
  DirMode = 2
  FaceMakerClass = Part::FaceMakerBullseye
  LengthFwd = 0
  LengthRev = 4
  Solid = true
  Symmetric = false
FEATURE [Sketcher::SketchObject] Sketch006  label="toggle switch ribs"
  MapMode = 5
  sketch-geometry (4):
    g0: LineSegment StartX=22 StartY=59 StartZ=0 EndX=22 EndY=37 EndZ=0
    g1: LineSegment StartX=22 StartY=59 StartZ=0 EndX=17 EndY=59 EndZ=0
    g2: LineSegment StartX=17 StartY=59 StartZ=0 EndX=17 EndY=37 EndZ=0
    g3: LineSegment StartX=17 StartY=37 StartZ=0 EndX=22 EndY=37 EndZ=0
  constraints (12):
    c: DistanceX(g-1,g0) = 22
    c: Vertical(g0)
    c: DistanceY(g0,g0) = 22
    c: Coincident(g1,g0)
    c: Horizontal(g1)
    c: DistanceX(g1,g1) = 5
    c: Coincident(g2,g1)
    c: Vertical(g2)
    c: Coincident(g3,g2)
    c: Coincident(g3,g0)
    c: Horizontal(g3)
    c: DistanceY(g-1,g2) = 37
FEATURE [Part::Extrusion] Extrude007  label="Extrude toggle switch ribs"
  Base = -> Sketch006
  Dir = (0,0,1)
  DirMode = 2
  FaceMakerClass = Part::FaceMakerBullseye
  LengthFwd = 0
  LengthRev = 10
  Solid = true
  Symmetric = false
FEATURE [Sketcher::SketchObject] Sketch007  label="panel cover"
  MapMode = 5
  sketch-geometry (30):
    g0: Circle CenterX=-84 CenterY=-45 CenterZ=0 NormalX=0 NormalY=0 NormalZ=1 AngleXU=0 Radius=5
    g1: LineSegment [constr] StartX=49 StartY=-50 StartZ=0 EndX=107 EndY=-50 EndZ=0
    g2: Circle [constr] CenterX=107 CenterY=-50 CenterZ=0 NormalX=0 NormalY=0 NormalZ=1 AngleXU=0 Radius=6.35
    g3: Circle CenterX=97 CenterY=7 CenterZ=0 NormalX=0 NormalY=0 NormalZ=1 AngleXU=0 Radius=5
    g4: Circle CenterX=-128 CenterY=0 CenterZ=0 NormalX=0 NormalY=0 NormalZ=1 AngleXU=0 Radius=2
    g5: Circle CenterX=128 CenterY=0 CenterZ=0 NormalX=0 NormalY=0 NormalZ=1 AngleXU=0 Radius=2
    g6: LineSegment [constr] StartX=30 StartY=48 StartZ=0 EndX=80 EndY=48 EndZ=0
    g7: Circle CenterX=30 CenterY=48 CenterZ=0 NormalX=0 NormalY=0 NormalZ=1 AngleXU=0 Radius=6.35
    g8: LineSegment StartX=47.85 StartY=-61.3 StartZ=0 EndX=50.15 EndY=-61.3 EndZ=0
    g9: LineSegment StartX=50.15 StartY=-61.3 StartZ=0 EndX=50.15 EndY=-60.2859 EndZ=0
    g10: LineSegment StartX=47.85 StartY=-61.3 StartZ=0 EndX=47.85 EndY=-60.2859 EndZ=0
    g11: ArcOfCircle CenterX=49 CenterY=-50 CenterZ=0 NormalX=0 NormalY=0 NormalZ=1 AngleXU=0 Radius=10.35 StartAngle=4.82373 EndAngle=10.8842
    g12: LineSegment StartX=78.85 StartY=36.7 StartZ=0 EndX=81.15 EndY=36.7 EndZ=0
    g13: LineSegment StartX=78.85 StartY=36.7 StartZ=0 EndX=78.85 EndY=37.7141 EndZ=0
    g14: LineSegment StartX=81.15 StartY=36.7 StartZ=0 EndX=81.15 EndY=37.7141 EndZ=0
    g15: ArcOfCircle CenterX=80 CenterY=48 CenterZ=0 NormalX=0 NormalY=0 NormalZ=1 AngleXU=0 Radius=10.35 StartAngle=4.82373 EndAngle=10.8842
    g16: ArcOfCircle CenterX=-123.32 CenterY=66.32 CenterZ=0 NormalX=0 NormalY=0 NormalZ=1 AngleXU=0 Radius=11.68 StartAngle=1.5708 EndAngle=3.14159
    g17: ArcOfCircle CenterX=123.32 CenterY=66.32 CenterZ=0 NormalX=0 NormalY=0 NormalZ=1 AngleXU=0 Radius=11.68 StartAngle=1.033e-13 EndAngle=1.5708
    g18: ArcOfCircle CenterX=123.32 CenterY=-66.32 CenterZ=0 NormalX=0 NormalY=0 NormalZ=1 AngleXU=0 Radius=11.68 StartAngle=4.71239 EndAngle=6.28319
    g19: ArcOfCircle CenterX=-123.32 CenterY=-66.32 CenterZ=0 NormalX=0 NormalY=0 NormalZ=1 AngleXU=0 Radius=11.68 StartAngle=3.14159 EndAngle=4.71239
    g20: LineSegment StartX=-123.32 StartY=78 StartZ=0 EndX=123.32 EndY=78 EndZ=0
    g21: LineSegment StartX=-135 StartY=66.32 StartZ=0 EndX=-135 EndY=-66.32 EndZ=0
    g22: LineSegment StartX=135 StartY=66.32 StartZ=0 EndX=135 EndY=-66.32 EndZ=0
    g23: LineSegment StartX=-123.32 StartY=-78 StartZ=0 EndX=123.32 EndY=-78 EndZ=0
    g24: LineSegment StartX=109.218 StartY=-59.2376 StartZ=0 EndX=116.238 EndY=-52.2176 EndZ=0
    g25: LineSegment StartX=97.7624 StartY=-47.7824 StartZ=0 EndX=104.782 EndY=-40.7624 EndZ=0
    g26: LineSegment [constr] StartX=101.272 StartY=-44.2724 StartZ=0 EndX=107 EndY=-50 EndZ=0
    g27: LineSegment [constr] StartX=107 StartY=-50 StartZ=0 EndX=112.728 EndY=-55.7276 EndZ=0
    g28: ArcOfCircle CenterX=107 CenterY=-50 CenterZ=0 NormalX=0 NormalY=0 NormalZ=1 AngleXU=0 Radius=9.5 StartAngle=2.90599 EndAngle=4.94799
    g29: ArcOfCircle CenterX=107 CenterY=-50 CenterZ=0 NormalX=0 NormalY=0 NormalZ=1 AngleXU=0 Radius=9.5 StartAngle=6.04758 EndAngle=8.08958
  constraints (85):
    c: Radius(g0) = 5
    c: Horizontal(g1)
    c: Coincident(g2,g1)
    c: Radius(g2) = 6.35
    c: PointOnObject(g4,g-1)
    c: PointOnObject(g5,g-1)
    c: Radius(g4) = 2
    c: Equal(g4,g5)
    c: Horizontal(g6)
    c: Coincident(g7,g6)
    c: Equal(g7,g2)
    c: Equal(g3,g0)
    c: DistanceX(g6,g6) = 50
    c: DistanceY(g-1,g6) = 48
    c: DistanceY(g1,g-1) = 50
    c: Horizontal(g8)
    c: DistanceX(g8,g8) = 2.3
    c: Coincident(g9,g8)
    c: Vertical(g9)
    c: Coincident(g10,g8)
    c: Vertical(g10)
    c: Coincident(g11,g10)
    c: Coincident(g11,g9)
    c: Radius(g11) = 10.35
    c: DistanceY(g8,g1) = 11.3
    c: Horizontal(g12)
    c: DistanceX(g12,g12) = 2.3
    c: DistanceX(g12,g6) = 1.15
    c: DistanceY(g12,g6) = 11.3
    c: Coincident(g13,g12)
    c: Vertical(g13)
    c: Coincident(g14,g12)
    c: Vertical(g14)
    c: Coincident(g15,g6)
    c: Coincident(g15,g13)
    c: Coincident(g15,g14)
    c: Radius(g15) = 10.35
    c: Coincident(g11,g1)
    c: Horizontal(g10,g9)
    c: DistanceX(g1,g1) = 58
    c: DistanceX(g-1,g6) = 30
    c: DistanceX(g-1,g3) = 97
    c: DistanceY(g-1,g3) = 7
    c: DistanceX(g4,g-1) = 128
    c: DistanceX(g0,g-1) = 84
    c: DistanceY(g0,g-1) = 45
    c: DistanceX(g-1,g5) = 128
    c: DistanceX(g-1,g1) = 49
    c: Radius(g16) = 11.68
    c: Equal(g16,g19)
    c: Equal(g19,g18)
    c: Equal(g18,g17)
    c: Horizontal(g20)
    c: Coincident(g20,g17)
    c: Vertical(g21)
    c: Vertical(g22)
    c: DistanceX(g16,g17) = 270
    c: Symmetric(g16,g17,g-2)
    c: DistanceY(g19,g16) = 156
    c: Symmetric(g19,g16,g-1)
    c: Tangent(g20,g16) = 1.5708
    c: Tangent(g21,g16) = -1.5708
    c: Tangent(g21,g19) = -1.5708
    c: Tangent(g23,g19) = -1.5708
    c: Tangent(g23,g18) = -1.5708
    c: Tangent(g18,g22) = 1.5708
    c: Tangent(g22,g17) = 1.5708
    c: PointOnObject(g26,g25)
    c: Coincident(g26,g1)
    c: Perpendicular(g26,g25)
    c: Angle(g24,g23) = 2.35619
    c: Parallel(g25,g24)
    c: Coincident(g27,g26)
    c: PointOnObject(g27,g24)
    c: Perpendicular(g27,g24)
    c: Distance(g27) = 8.1
    c: Equal(g26,g27)
    c: Coincident(g28,g1)
    c: Coincident(g28,g25)
    c: Coincident(g28,g24)
    c: Coincident(g29,g28)
    c: Coincident(g29,g25)
    c: Coincident(g29,g24)
    c: Diameter(g29) = 19
    c: Equal(g28,g29)
FEATURE [Part::Extrusion] Extrude008  label="Extrude panel surface"
  Base = -> Sketch
  Dir = (0,0,1)
  DirMode = 2
  FaceMakerClass = Part::FaceMakerBullseye
  LengthFwd = 3
  LengthRev = 0
  Solid = true
  Symmetric = false
FEATURE [Sketcher::SketchObject] Sketch008  label="lcd cavity"
  MapMode = 5
  sketch-geometry (13):
    g0: LineSegment [constr] StartX=-117 StartY=65 StartZ=0 EndX=-2.7 EndY=65 EndZ=0
    g1: LineSegment [constr] StartX=-2.7 StartY=65 StartZ=0 EndX=-2.7 EndY=-14.375 EndZ=0
    g2: LineSegment [constr] StartX=-2.7 StartY=-14.375 StartZ=0 EndX=-117 EndY=-14.375 EndZ=0
    g3: LineSegment [constr] StartX=-117 StartY=-14.375 StartZ=0 EndX=-117 EndY=65 EndZ=0
    g4: LineSegment [constr] StartX=-117 StartY=30.075 StartZ=0 EndX=-2.7 EndY=30.075 EndZ=0
    g5: LineSegment [constr] StartX=-97.95 StartY=65 StartZ=0 EndX=-97.95 EndY=-14.375 EndZ=0
    g6: LineSegment [constr] StartX=-63.66 StartY=65 StartZ=0 EndX=-63.66 EndY=-14.375 EndZ=0
    g7: LineSegment [constr] StartX=-23.02 StartY=65 StartZ=0 EndX=-23.02 EndY=-14.375 EndZ=0
    g8: LineSegment [constr] StartX=-117 StartY=61.825 StartZ=0 EndX=-2.7 EndY=61.825 EndZ=0
    g9: LineSegment StartX=-115.95 StartY=57.075 StartZ=0 EndX=-5.02 EndY=57.075 EndZ=0
    g10: LineSegment StartX=-5.02 StartY=57.075 StartZ=0 EndX=-5.02 EndY=3.075 EndZ=0
    g11: LineSegment StartX=-5.02 StartY=3.075 StartZ=0 EndX=-115.95 EndY=3.075 EndZ=0
    g12: LineSegment StartX=-115.95 StartY=3.075 StartZ=0 EndX=-115.95 EndY=57.075 EndZ=0
  constraints (43):
    c: Coincident(g0,g1)
    c: Coincident(g1,g2)
    c: Coincident(g2,g3)
    c: Coincident(g3,g0)
    c: Horizontal(g0)
    c: Horizontal(g2)
    c: Vertical(g1)
    c: Vertical(g3)
    c: DistanceX(g0,g0) = 114.3
    c: DistanceY(g1,g1) = 79.375
    c: PointOnObject(g4,g3)
    c: PointOnObject(g4,g1)
    c: DistanceY(g4,g0) = 34.925
    c: PointOnObject(g5,g0)
    c: PointOnObject(g5,g2)
    c: Vertical(g5)
    c: DistanceX(g5,g1) = 95.25
    c: PointOnObject(g6,g0)
    c: PointOnObject(g6,g2)
    c: Vertical(g6)
    c: DistanceX(g6,g1) = 60.96
    c: PointOnObject(g7,g0)
    c: PointOnObject(g7,g2)
    c: Vertical(g7)
    c: DistanceX(g7,g1) = 20.32
    c: PointOnObject(g8,g3)
    c: PointOnObject(g8,g1)
    c: Horizontal(g8)
    c: DistanceY(g8,g0) = 3.175
    c: DistanceY(g-1,g0) = 65
    c: DistanceX(g1,g-1) = 2.7
    c: Coincident(g9,g10)
    c: Coincident(g10,g11)
    c: Coincident(g11,g12)
    c: Coincident(g12,g9)
    c: Horizontal(g9)
    c: Horizontal(g11)
    c: Vertical(g10)
    c: Vertical(g12)
    c: DistanceY(g12,g12) = 54
    c: Symmetric(g11,g9,g4)
    c: DistanceX(g11,g5) = 18
    c: DistanceX(g7,g10) = 18
FEATURE [Part::Extrusion] Extrude009  label="Extrude lcd cavity"
  Base = -> Sketch008
  Dir = (0,0,1)
  DirMode = 2
  FaceMakerClass = Part::FaceMakerBullseye
  LengthFwd = 5
  LengthRev = 0
  Placement = pos=(0,0,-6.3) rot=(0,0,1;0rad)
  Solid = true
  Symmetric = false
FEATURE [Part::MultiFuse] Fusion
  Shapes = -> [Extrude005,Extrude]
FEATURE [Part::Cut] Cut  label="ribs and nibs with cavity"
  Base = -> Fusion
  Tool = -> Extrude009
FEATURE [Sketcher::SketchObject] Sketch009  label="shaft recesses"
  MapMode = 5
  sketch-geometry (3):
    g0: Circle CenterX=-84 CenterY=-45 CenterZ=0 NormalX=0 NormalY=0 NormalZ=1 AngleXU=0 Radius=14
    g1: Circle CenterX=97 CenterY=7 CenterZ=0 NormalX=0 NormalY=0 NormalZ=1 AngleXU=0 Radius=14
    g2: Circle CenterX=107 CenterY=-50 CenterZ=0 NormalX=0 NormalY=0 NormalZ=1 AngleXU=0 Radius=14
  constraints (9):
    c: Radius(g0) = 14
    c: Equal(g1,g0)
    c: DistanceX(g0,g-1) = 84
    c: DistanceY(g0,g-1) = 45
    c: DistanceX(g-1,g1) = 97
    c: DistanceY(g-1,g1) = 7
    c: Equal(g1,g2)
    c: DistanceX(g-1,g2) = 107
    c: DistanceY(g2,g-1) = 50
FEATURE [Part::Extrusion] Extrude010  label="Extrude shaft recesses"
  Base = -> Sketch009
  Dir = (0,0,1)
  DirMode = 2
  FaceMakerClass = Part::FaceMakerBullseye
  LengthFwd = 1
  LengthRev = 0
  Solid = true
  Symmetric = false
FEATURE [Part::Cut] Cut001  label="panel with shaft recesses"
  Base = -> Extrude008
  Tool = -> Extrude010
FEATURE [Part::MultiFuse] Fusion001  label="3D printable panel"
  Shapes = -> [Cut001,Cut,Extrude002,Extrude006,Extrude007]
FEATURE [Part::Extrusion] Extrude011  label="Extrude panel cover"
  Base = -> Sketch007
  Dir = (0,0,1)
  DirMode = 2
  FaceMakerClass = Part::FaceMakerBullseye
  LengthFwd = 1.5875
  LengthRev = 0
  Solid = true
  Symmetric = false
FEATURE [App::FeaturePython] SetupSheet  # Path/CAM operation (typed FeaturePython)
  ClearanceHeightExpression = StartDepth+SetupSheet.ClearanceHeightOffset
  ClearanceHeightOffset = 5
  FinalDepthExpression = OpFinalDepth
  HorizRapid = 0
  SafeHeightExpression = StartDepth+SetupSheet.SafeHeightOffset
  SafeHeightOffset = 3
  StartDepthExpression = OpStartDepth
  StepDownExpression = OpToolDiameter
  VertRapid = 0
FEATURE [Part::FeaturePython] Clone  label="Base-Extrude panel cover"  # Draft clone (typed FeaturePython)
  AttacherType = Attacher::AttachEngine3D
  Fuse = false
  Objects = -> [Extrude011]
  PathResource = Base
  Scale = (1,1,1)
FEATURE [Part::FeaturePython] Stock  # WARN: FeaturePython — macro-defined, semantics opaque (R4)
  Base = -> Extrude011
  ExtXneg = 1
  ExtXpos = 1
  ExtYneg = 1
  ExtYpos = 1
  ExtZneg = 1
  ExtZpos = 1
  StockType = FromBase
FEATURE [Path::FeaturePython] T1__1_16__single_flute_end_mill  label="T1: 1/16" single-flute end mill"  # Path/CAM operation (typed FeaturePython)
  HorizFeed = 12
  HorizRapid = 0
  SpindleDir = 0
  SpindleSpeed = 18000
  ToolNumber = 1
  VertFeed = 1
  VertRapid = 0
  expr: HorizRapid = SetupSheet.HorizRapid
  expr: VertRapid = SetupSheet.VertRapid
FEATURE [Path::FeaturePython] Profile_Edges  # Path/CAM operation (typed FeaturePython)
  Active = true
  AreaParams:
    OpenMode = 0
    Angle = 45.0
    MinArcPoints = 4
    Coplanar = 0
    Tolerance = 1e-07
    CleanDistance = 0.0
    PocketExtraOffset = 0.0
    RoundPrecision = 0.0
    AngleShift = 0.0
    SubjectFill = 0
    PocketMode = 0
    PocketLastStepover = 0.0
    Simplify = False
    SectionTolerance = 1e-06
    MaxArcPoints = 100
    Offset = -0.795
    Accuracy = 0.01
    LastStepover = 0.0
    PocketStepover = 0.0
    ClipFill = 0
    ToolRadius = 1.0
    Outline = False
    ClipperScale = 10000000.0
    FromCenter = False
    Explode = False
    EndType = 0
    Shift = 0.0
    ExtraPass = 0
    Project = False
    JoinType = 0
    Thicken = False
    Stepdown = 1.0
    SectionMode = 2
    MiterLimit = 2.0
    Deflection = 0.01
    Reorient = True
    FitArcs = True
    SectionCount = -1
    SectionOffset = 0.0
    Stepover = 0.0
    Unit = 1.0
    Fill = 0
  Base = -> [Clone]
  ClearanceHeight = 5
  Direction = 0
  FinalDepth = -3
  JoinType = 0
  MiterLimit = 0.1
  OffsetExtra = 0
  OpFinalDepth = 1.5875
  OpStartDepth = 2.5875
  OpStockZMax = 2.5875
  OpStockZMin = -1
  OpToolDiameter = 1.59
  PathParams = {'resume_height': 3.0, 'feedrate': 12.0, 'verbose': True, 'orientation': 1, 'return_end': True, 'preamble': False, 'retraction': 5.0, 'feedrate_v': 1.0}
  SafeHeight = 3
  Side = 1
  StartDepth = 0
  StartPoint = (0,0,0)
  StepDown = 4
  ToolController = -> T1__1_16__single_flute_end_mill
  UseComp = true
  UseStartPoint = false
  expr: ClearanceHeight = StartDepth + SetupSheet.ClearanceHeightOffset
  expr: SafeHeight = StartDepth + SetupSheet.SafeHeightOffset
  expr: StepDown = 4
  expr: FinalDepth = -3
  expr: StartDepth = 0
FEATURE [Path::FeaturePython] Contour  # Path/CAM operation (typed FeaturePython)
  Active = true
  AreaParams:
    OpenMode = 0
    Angle = 45.0
    MinArcPoints = 4
    Coplanar = 2
    Tolerance = 1e-07
    CleanDistance = 0.0
    PocketExtraOffset = 0.0
    RoundPrecision = 0.0
    AngleShift = 0.0
    SubjectFill = 0
    PocketMode = 0
    Simplify = False
    SectionTolerance = 1e-06
    MaxArcPoints = 100
    Offset = 0.795
    Accuracy = 0.01
    PocketStepover = 0.0
    ClipFill = 0
    ToolRadius = 1.0
    Outline = False
    ClipperScale = 10000000.0
    FromCenter = False
    Explode = False
    EndType = 0
    Shift = 0.0
    ExtraPass = 0
    Project = False
    JoinType = 0
    Thicken = False
    Stepdown = 1.0
    SectionMode = 2
    MiterLimit = 2.0
    Deflection = 0.01
    Reorient = True
    FitArcs = True
    SectionCount = -1
    SectionOffset = 0.0
    Stepover = 0.0
    Unit = 1.0
    Fill = 0
  ClearanceHeight = 5
  Direction = 0
  FinalDepth = -3
  JoinType = 0
  MiterLimit = 0.1
  OffsetExtra = 0
  OpFinalDepth = -1
  OpStartDepth = 2.5875
  OpStockZMax = 0
  OpStockZMin = 0
  OpToolDiameter = 1.59
  PathParams = {'resume_height': 3.0, 'feedrate': 12.0, 'verbose': True, 'orientation': 1, 'return_end': True, 'preamble': False, 'retraction': 5.0, 'feedrate_v': 1.0}
  SafeHeight = 3
  Side = 0
  StartDepth = 0
  StartPoint = (0,0,0)
  StepDown = 4
  ToolController = -> T1__1_16__single_flute_end_mill
  UseComp = true
  UseStartPoint = false
  expr: ClearanceHeight = StartDepth + SetupSheet.ClearanceHeightOffset
  expr: SafeHeight = StartDepth + SetupSheet.SafeHeightOffset
  expr: StepDown = 4
  expr: FinalDepth = -3
  expr: StartDepth = 0
FEATURE [Mesh::FeaturePython] CutMaterial  # WARN: FeaturePython — macro-defined, semantics opaque (R4)
FEATURE [App::DocumentObjectGroup] Model  label="Unnamed001"
  Group = -> [Clone]
FEATURE [Path::FeatureCompoundPython] Operations001  label="Operations"  # Path/CAM operation (typed FeaturePython)
  Group = -> [Profile_Edges,Contour]
  UsePlacements = false
FEATURE [Path::FeaturePython] Job  label="CNC route panel cover"  # Path/CAM operation (typed FeaturePython)
  GeometryTolerance = 0.01
  Model = -> Model
  Operations = -> Operations001
  PostProcessor = 5
  PostProcessorOutputFile = <userpath>/geda/altusmetrum/mechanical/telelco_1170_panel_cover.ngc
  SetupSheet = -> SetupSheet
  Stock = -> Stock
  ToolController = -> [T1__1_16__single_flute_end_mill]
